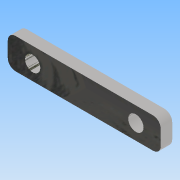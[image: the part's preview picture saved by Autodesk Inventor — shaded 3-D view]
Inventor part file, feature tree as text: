
AUTODESK INVENTOR PART (.ipt)
format: ipt  version: 2015 (Build 190159000, 159)  size: 99,328 bytes
history: native  units: mm
features: extrude x1, fillet x1, sketch x1
ambient origin geometry x8: Origin, YZ Plane, XZ Plane, XY Plane, X Axis, Y Axis, Z Axis, Center Point
bodies: Solide1 (feature_tree)
feature tree (3):
  extrude  "Extrusion1"  Depth=8.0mm
  fillet  "Congé1"  Radius=40.0mm
  sketch  "Esquisse1"
